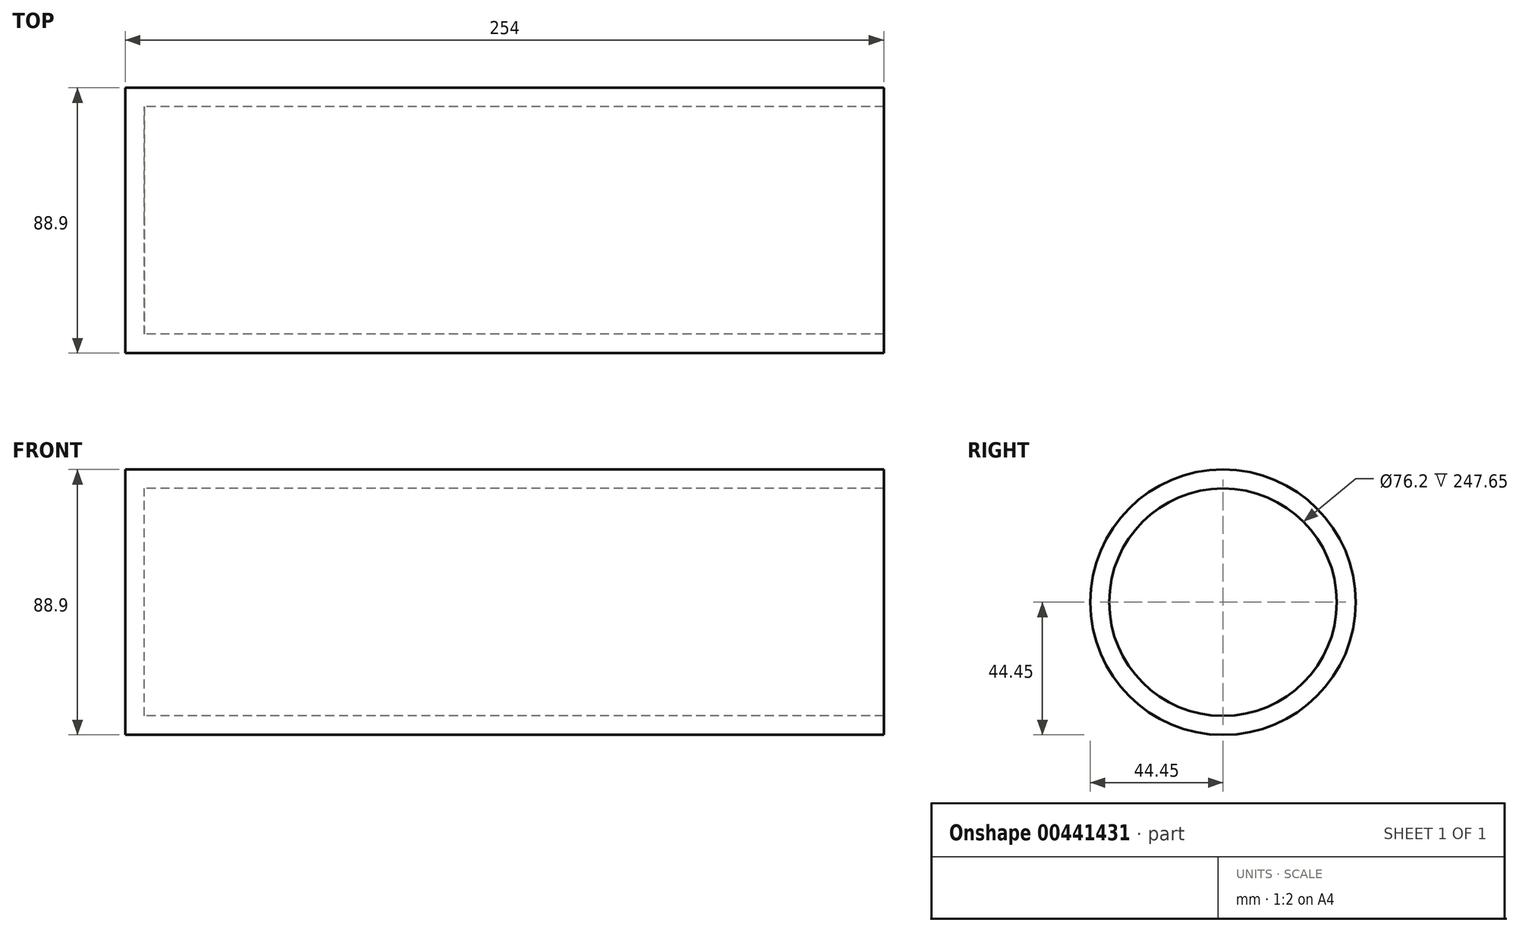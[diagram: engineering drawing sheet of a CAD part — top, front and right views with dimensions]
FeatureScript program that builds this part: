
annotation { "Feature Type Name" : "Feature", "Feature Type Description" : "" }
export const myFeature = defineFeature(function(context is Context, id is Id, definition is map)
    precondition{}
    {
        {
            var Q0;
            Q0=qCreatedBy(makeId("Right.planeOp"),FACE);
            var sketch = newSketch(context, id + "F0", { "sketchPlane" : qUnion([Q0])});
            skCircle(sketch, "E0", {"center": v(0, 0) * mm, "radius": 44.45 * mm});
            skSolve(sketch);
        }
        {
            var Q0;
            Q0 = qSketchRegion(id + "F0", true);
            extrude(context, id + "F1", {"entities" : qUnion([Q0]), "depth" : 127 * mm, "hasSecondDirection" : true, "secondDirectionOppositeDirection" : true, "secondDirectionDepth" : 127 * mm});
        }
        {
            var Q0;
            Q0=makeQuery(id+"F1.opExtrude","CAP_FACE",FACE,{"disambiguationData":[OSD([sQuery(id+"F0.wireOp",EDGE,"E0")])],"isStart":false});
            shell(context, id + "F2", {"entities" : qUnion([Q0]), "thickness" : 6.35 * mm});
        }
    });
